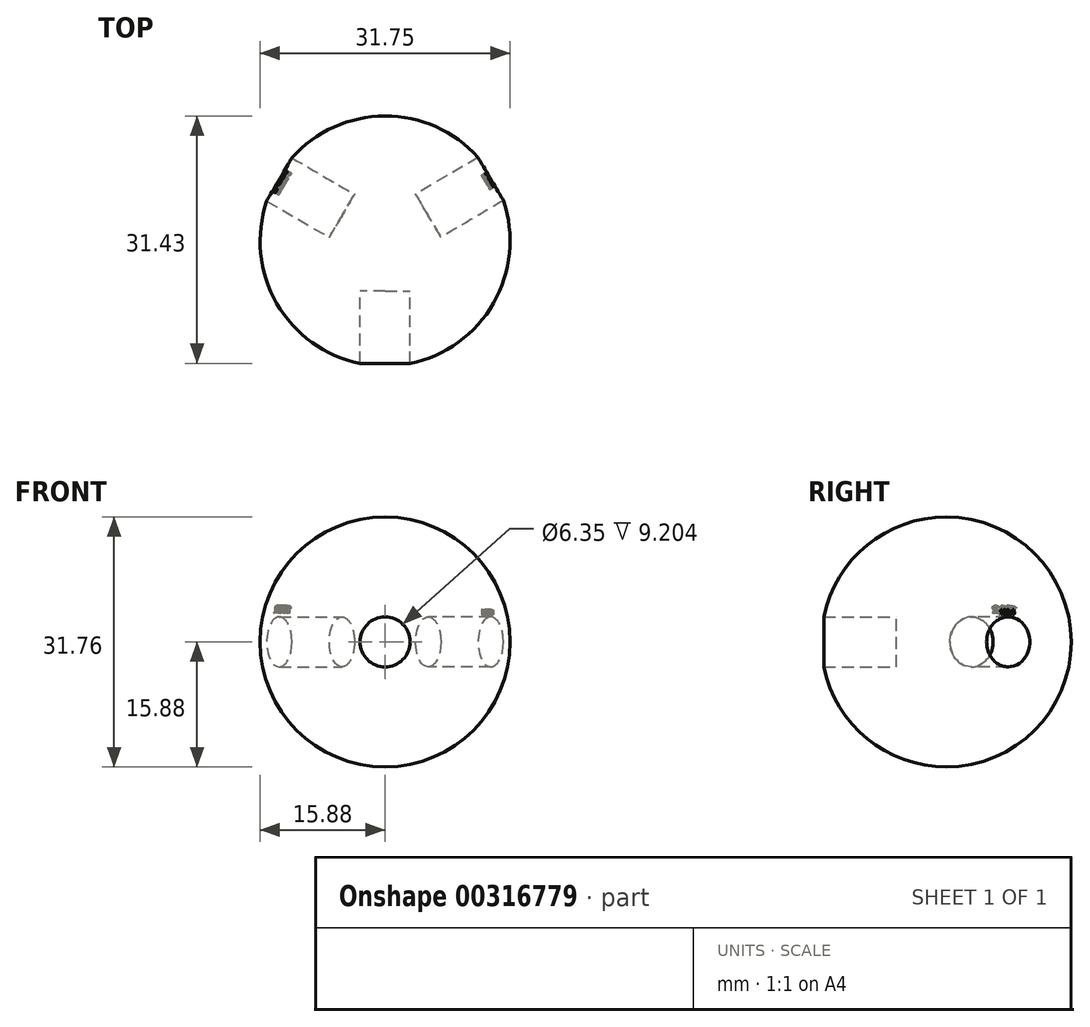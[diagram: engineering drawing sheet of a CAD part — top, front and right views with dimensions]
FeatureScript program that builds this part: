
annotation { "Feature Type Name" : "Feature", "Feature Type Description" : "" }
export const myFeature = defineFeature(function(context is Context, id is Id, definition is map)
    precondition{}
    {
        {
            var Q0;
            Q0=qCreatedBy(makeId("Front.planeOp"),FACE);
            var sketch = newSketch(context, id + "F0", { "sketchPlane" : qUnion([Q0])});
            skArc(sketch, "E0", {"start": v(0, 15.88) * mm, "mid": v(-15.88, 0) * mm, "end": v(0, -15.88) * mm});
            skLineSegment(sketch, "E1", {"start": v(0, 15.88) * mm, "end": v(0, -15.88) * mm});
            skSolve(sketch);
        }
        {
            var Q0;
            Q0=qCreatedBy(makeId("Top.planeOp"),FACE);
            var sketch = newSketch(context, id + "F1", { "sketchPlane" : qUnion([Q0])});
            skCircle(sketch, "E2", {"center": v(0, 0) * mm, "radius": 15.88 * mm});
            skSolve(sketch);
        }
        {
            var Q0;
            Q0=makeQuery(id+"F0.imprint","IMPRINT",FACE,{"disambiguationData":[TD([[makeQuery(id+"F0.imprint","IMPRINT",EDGE,{"derivedFrom":sQuery(id+"F0.wireOp",EDGE,"E0")}),1.0]])]});
            var Q1;
            Q1=sQuery(id+"F1.wireOp",EDGE,"E2");
            revolve(context, id + "F2", {"entities" : qUnion([Q0]), "axis" : qUnion([Q1]), "revolveType" : RevolveType.FULL});
        }
        {
            var Q0;
            Q0=qCreatedBy(makeId("Front.planeOp"),FACE);
            cPlane(context, id + "F3", {"entities" : qUnion([Q0]), "cplaneType" : CPlaneType.OFFSET, "offset" : 6.35 * mm, "width" : 152.4 * mm, "height" : 152.4 * mm});
        }
        {
            var Q0;
            Q0=qCreatedBy(id+"F3.planeOp",FACE);
            var sketch = newSketch(context, id + "F4", { "sketchPlane" : qUnion([Q0])});
            skCircle(sketch, "E3", {"center": v(0, 0) * mm, "radius": 3.18 * mm});
            skSolve(sketch);
        }
        {
            var Q0;
            Q0=qSketchRegion(id+"F4",true);
            extrude(context, id + "F5", {"entities" : qUnion([Q0]), "depth" : 25.4 * mm});
        }
        {
            var Q0;
            Q0=qCreatedBy(makeId("Right.planeOp"),FACE);
            var sketch = newSketch(context, id + "F6", { "sketchPlane" : qUnion([Q0])});
            skLineSegment(sketch, "E4", {"start": v(0, 67.47) * mm, "end": v(0, -53.83) * mm, "construction": true});
            skSolve(sketch);
        }
        {
            var Q0;
            Q0=qCreatedBy(makeId("Top.planeOp"),FACE);
            var sketch = newSketch(context, id + "F7", { "sketchPlane" : qUnion([Q0])});
            skLineSegment(sketch, "E5", {"start": v(69.95, 0) * mm, "end": v(-61.3, 0) * mm, "construction": true});
            skSolve(sketch);
        }
        {
            var Q0;
            Q0=makeQuery(id+"F5.opExtrude","SWEPT_BODY",BODY,{"disambiguationData":[OSD([sQuery(id+"F4.wireOp",EDGE,"E3")])]});
            var Q1;
            Q1=sQuery(id+"F7.wireOp",EDGE,"E5");
            transform(context, id + "F8", {"entities" : qUnion([Q0]), "transformType" : TransformType.ROTATION, "transformAxis" : qUnion([Q1]), "angle" : 119.9 * degree, "makeCopy" : true});
        }
        {
            var Q0;
            Q0=makeQuery(id+"F5.opExtrude","SWEPT_BODY",BODY,{"disambiguationData":[OSD([sQuery(id+"F4.wireOp",EDGE,"E3")])]});
            var Q1;
            Q1=sQuery(id+"F7.wireOp",EDGE,"E5");
            transform(context, id + "F9", {"entities" : qUnion([Q0]), "transformType" : TransformType.ROTATION, "transformAxis" : qUnion([Q1]), "angle" : 120.7 * degree, "oppositeDirection" : true, "makeCopy" : true});
        }
        {
            var Q0;
            Q0=makeQuery(id+"F5.opExtrude","SWEPT_BODY",BODY,{"disambiguationData":[OSD([sQuery(id+"F4.wireOp",EDGE,"E3")])]});
            var Q1;
            Q1=sQuery(id+"F6.wireOp",EDGE,"E4");
            transform(context, id + "F10", {"entities" : qUnion([Q0]), "transformType" : TransformType.ROTATION, "transformAxis" : qUnion([Q1]), "angle" : 120.2 * degree, "makeCopy" : true});
        }
        {
            var Q0;
            Q0=makeQuery(id+"F10.opPattern","COPY",FACE,{"derivedFrom":makeQuery(id+"F5.opExtrude","CAP_FACE",FACE,{"disambiguationData":[OSD([sQuery(id+"F4.wireOp",EDGE,"E3")])],"isStart":false}),"instanceName":"1"});
            cPlane(context, id + "F11", {"entities" : qUnion([Q0]), "cplaneType" : CPlaneType.OFFSET, "offset" : 15.04 * mm, "oppositeDirection" : true, "width" : 152.4 * mm, "height" : 152.4 * mm});
        }
        {
            var Q0;
            Q0=qCreatedBy(id+"F11.planeOp",FACE);
            var sketch = newSketch(context, id + "F12", { "sketchPlane" : qUnion([Q0])});
            skText(sketch, "E6", { "text": "120.2", "fontName": "OpenSans-Bold.ttf"});
            const initialGuessF12  = {"E6": [-0.00153, 0.00367, 1, 0, 0.00093]};
            skSetInitialGuess(sketch, initialGuessF12);
            skSolve(sketch);
        }
        {
            var Q0;
            Q0 = qSketchRegion(id + "F12", true);
            extrude(context, id + "F13", {"entities" : qUnion([Q0]), "operationType" : NewBodyOperationType.REMOVE, "oppositeDirection" : true, "depth" : 2.08 * mm});
        }
        {
            var Q0;
            Q0=makeQuery(id+"F10.opPattern","COPY",BODY,{"derivedFrom":makeQuery(id+"F5.opExtrude","SWEPT_BODY",BODY,{"disambiguationData":[OSD([sQuery(id+"F4.wireOp",EDGE,"E3")])]}),"instanceName":"1"});
            var Q1;
            Q1=makeQuery(id+"F2.opRevolve","SWEPT_BODY",BODY,{"disambiguationData":[OSD([sQuery(id+"F0.wireOp",EDGE,"E0"),sQuery(id+"F0.wireOp",EDGE,"E1")])]});
            booleanBodies(context, id + "F14", {"operationType" : BooleanOperationType.SUBTRACTION, "tools" : qUnion([Q0]), "targets" : qUnion([Q1])});
        }
        {
            var Q0;
            Q0=makeQuery(id+"F5.opExtrude","SWEPT_BODY",BODY,{"disambiguationData":[OSD([sQuery(id+"F4.wireOp",EDGE,"E3")])]});
            var Q1;
            Q1=sQuery(id+"F6.wireOp",EDGE,"E4");
            transform(context, id + "F15", {"entities" : qUnion([Q0]), "transformType" : TransformType.ROTATION, "transformAxis" : qUnion([Q1]), "angle" : 120.4 * degree, "oppositeDirection" : true, "makeCopy" : true});
        }
        {
            var Q0;
            Q0=makeQuery(id+"F15.opPattern","COPY",FACE,{"derivedFrom":makeQuery(id+"F5.opExtrude","CAP_FACE",FACE,{"disambiguationData":[OSD([sQuery(id+"F4.wireOp",EDGE,"E3")])],"isStart":false}),"instanceName":"1"});
            cPlane(context, id + "F16", {"entities" : qUnion([Q0]), "cplaneType" : CPlaneType.OFFSET, "offset" : 14.76 * mm, "oppositeDirection" : true, "width" : 152.4 * mm, "height" : 152.4 * mm});
        }
        {
            var Q0;
            Q0=qCreatedBy(id+"F16.planeOp",FACE);
            var sketch = newSketch(context, id + "F17", { "sketchPlane" : qUnion([Q0])});
            skText(sketch, "E7", { "text": "120.4", "fontName": "OpenSans-Bold.ttf"});
            const initialGuessF17  = {"E7": [-0.00112, 0.0035, 1, 0, 0.0006]};
            skSetInitialGuess(sketch, initialGuessF17);
            skSolve(sketch);
        }
        {
            var Q0;
            Q0 = qSketchRegion(id + "F17", true);
            extrude(context, id + "F18", {"entities" : qUnion([Q0]), "operationType" : NewBodyOperationType.REMOVE, "oppositeDirection" : true, "depth" : 2.2 * mm});
        }
        {
            var Q0;
            Q0=makeQuery(id+"F15.opPattern","COPY",BODY,{"derivedFrom":makeQuery(id+"F5.opExtrude","SWEPT_BODY",BODY,{"disambiguationData":[OSD([sQuery(id+"F4.wireOp",EDGE,"E3")])]}),"instanceName":"1"});
            var Q1;
            Q1=makeQuery(id+"F2.opRevolve","SWEPT_BODY",BODY,{"disambiguationData":[OSD([sQuery(id+"F0.wireOp",EDGE,"E0"),sQuery(id+"F0.wireOp",EDGE,"E1")])]});
            booleanBodies(context, id + "F19", {"operationType" : BooleanOperationType.SUBTRACTION, "tools" : qUnion([Q0]), "targets" : qUnion([Q1])});
        }
        {
            var Q0;
            Q0=makeQuery(id+"F5.opExtrude","SWEPT_BODY",BODY,{"disambiguationData":[OSD([sQuery(id+"F4.wireOp",EDGE,"E3")])]});
            var Q1;
            Q1=makeQuery(id+"F2.opRevolve","SWEPT_BODY",BODY,{"disambiguationData":[OSD([sQuery(id+"F0.wireOp",EDGE,"E0"),sQuery(id+"F0.wireOp",EDGE,"E1")])]});
            booleanBodies(context, id + "F20", {"operationType" : BooleanOperationType.SUBTRACTION, "tools" : qUnion([Q0]), "targets" : qUnion([Q1])});
        }
        {
            var Q0;
            Q0=makeQuery(id+"F8.opPattern","COPY",BODY,{"derivedFrom":makeQuery(id+"F5.opExtrude","SWEPT_BODY",BODY,{"disambiguationData":[OSD([sQuery(id+"F4.wireOp",EDGE,"E3")])]}),"instanceName":"1"});
            deleteBodies(context, id + "F21", {"entities" : qUnion([Q0])});
        }
        {
            var Q0;
            Q0=makeQuery(id+"F9.opPattern","COPY",BODY,{"derivedFrom":makeQuery(id+"F5.opExtrude","SWEPT_BODY",BODY,{"disambiguationData":[OSD([sQuery(id+"F4.wireOp",EDGE,"E3")])]}),"instanceName":"1"});
            deleteBodies(context, id + "F22", {"entities" : qUnion([Q0])});
        }
    });
